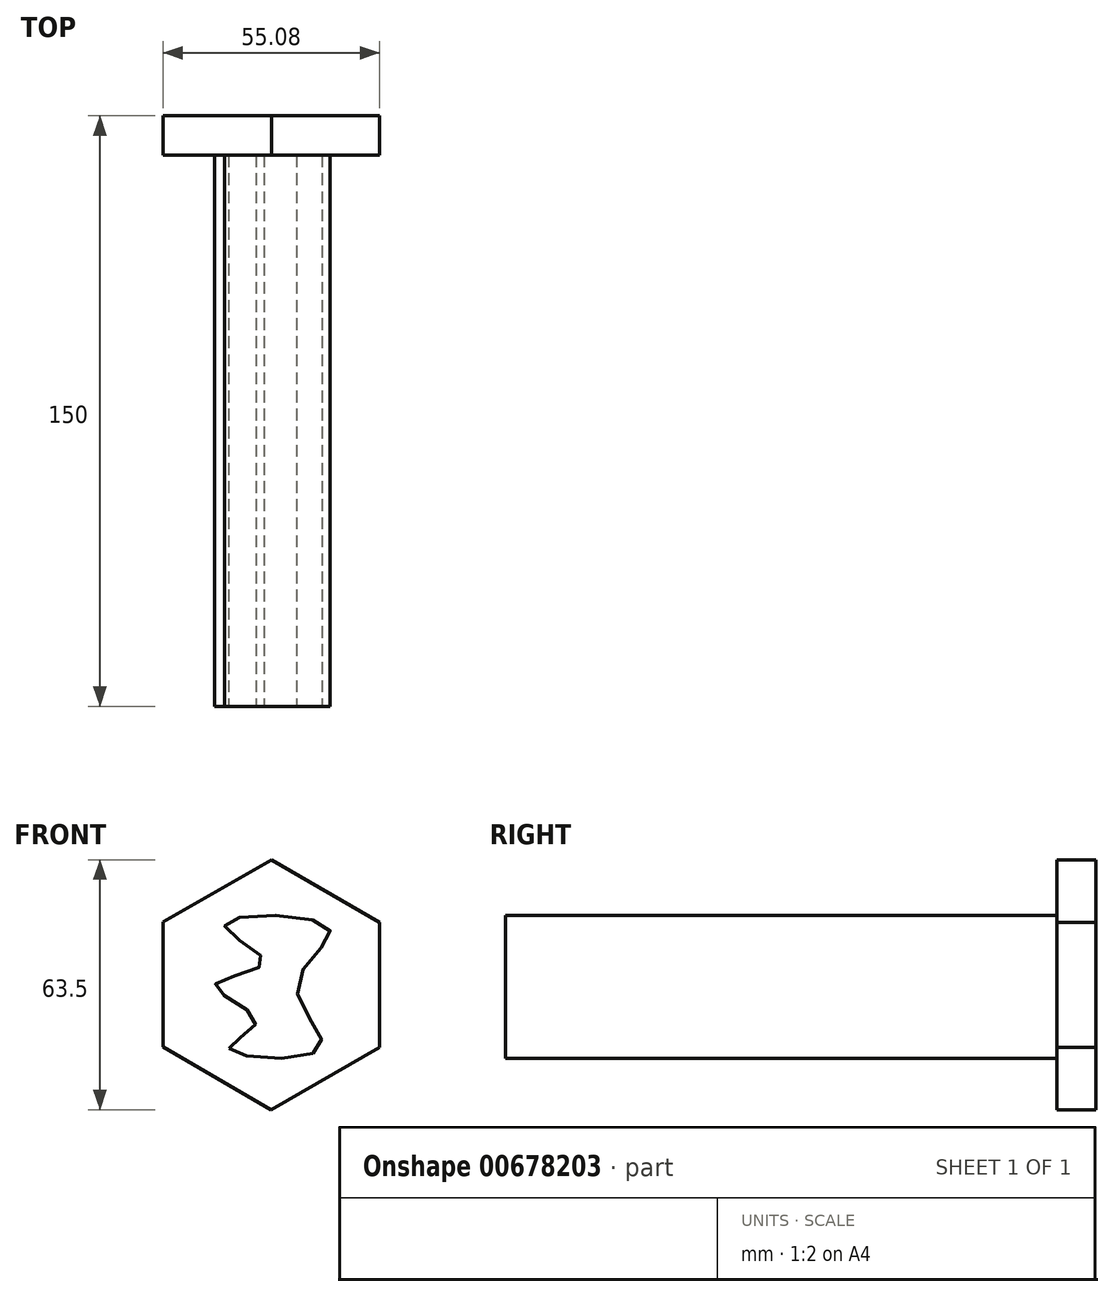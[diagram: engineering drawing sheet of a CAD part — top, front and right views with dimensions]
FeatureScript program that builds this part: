
annotation { "Feature Type Name" : "Feature", "Feature Type Description" : "" }
export const myFeature = defineFeature(function(context is Context, id is Id, definition is map)
    precondition{}
    {
        {
            var Q0;
            Q0=qCreatedBy(makeId("Front.planeOp"),FACE);
            var sketch = newSketch(context, id + "F0", { "sketchPlane" : qUnion([Q0])});
            skFitSpline(sketch, "E0", {"points": [v(-10.79, -16.23) * mm, v(12.32, -16.3) * mm, v(6.48, -0.14) * mm, v(14.57, 14.5) * mm, v(-11.85, 15.25) * mm, v(-1.9, 5.68) * mm, v(-14.35, -0.14) * mm, v(-3.85, -9.27) * mm, v(-10.79, -16.23) * mm]});
            skCircle(sketch, "E1.cCircle", {"center": v(0, 0) * mm, "radius": 31.75 * mm, "construction": true});
            skLineSegment(sketch, "E1.0", {"start": v(-27.45, 15.95) * mm, "end": v(0.1, 31.75) * mm});
            skLineSegment(sketch, "E1.1", {"start": v(0.1, 31.75) * mm, "end": v(27.54, 15.8) * mm});
            skLineSegment(sketch, "E1.2", {"start": v(27.54, 15.8) * mm, "end": v(27.45, -15.95) * mm});
            skLineSegment(sketch, "E1.3", {"start": v(27.45, -15.95) * mm, "end": v(-0.1, -31.75) * mm});
            skLineSegment(sketch, "E1.4", {"start": v(-0.1, -31.75) * mm, "end": v(-27.54, -15.8) * mm});
            skLineSegment(sketch, "E1.5", {"start": v(-27.54, -15.8) * mm, "end": v(-27.45, 15.95) * mm});
            skSolve(sketch);
        }
        {
            var Q0;
            Q0=makeQuery(id+"F0.imprint","IMPRINT",FACE,{"disambiguationData":[TD([[makeQuery(id+"F0.imprint","IMPRINT",EDGE,{"derivedFrom":sQuery(id+"F0.wireOp",EDGE,"E0")}),1.0]])]});
            extrude(context, id + "F1", {"entities" : qUnion([Q0]), "depth" : 150 * mm, "offsetDistance" : 25 * mm});
        }
        {
            var Q0;
            Q0=makeQuery(id+"F0.imprint","IMPRINT",FACE,{"disambiguationData":[TD([[makeQuery(id+"F0.imprint","IMPRINT",EDGE,{"derivedFrom":sQuery(id+"F0.wireOp",EDGE,"E0")}),-1.0]])]});
            extrude(context, id + "F2", {"entities" : qUnion([Q0]), "operationType" : NewBodyOperationType.ADD, "depth" : 10 * mm, "offsetDistance" : 25 * mm});
        }
    });
